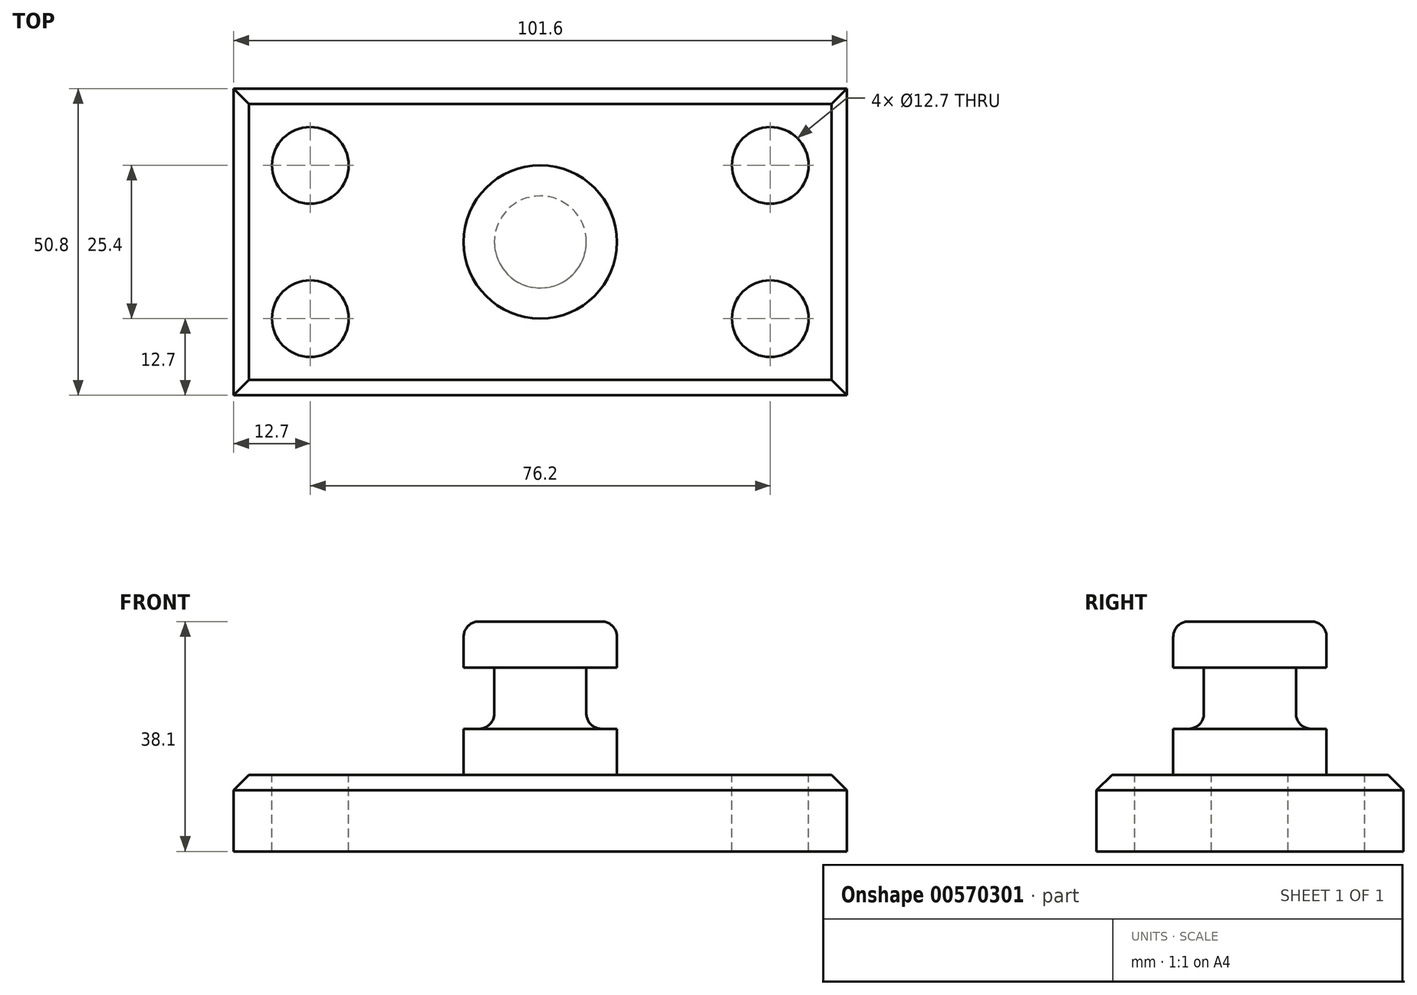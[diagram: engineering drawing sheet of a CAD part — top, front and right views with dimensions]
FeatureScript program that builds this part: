
annotation { "Feature Type Name" : "Feature", "Feature Type Description" : "" }
export const myFeature = defineFeature(function(context is Context, id is Id, definition is map)
    precondition{}
    {
        {
            var Q0;
            Q0=qCreatedBy(makeId("Top.planeOp"),FACE);
            var sketch = newSketch(context, id + "F0", { "sketchPlane" : qUnion([Q0])});
            skLineSegment(sketch, "E0.bottom", {"start": v(50.8, -25.4) * mm, "end": v(-50.8, -25.4) * mm});
            skLineSegment(sketch, "E0.top", {"start": v(50.8, 25.4) * mm, "end": v(-50.8, 25.4) * mm});
            skLineSegment(sketch, "E0.left", {"start": v(50.8, -25.4) * mm, "end": v(50.8, 25.4) * mm});
            skLineSegment(sketch, "E0.right", {"start": v(-50.8, -25.4) * mm, "end": v(-50.8, 25.4) * mm});
            skPoint(sketch, "E0.middle", {"position": v(0, 0) * mm});
            skSolve(sketch);
        }
        {
            var Q0;
            Q0 = qSketchRegion(id + "F0", true);
            extrude(context, id + "F1", {"entities" : qUnion([Q0]), "depth" : 12.7 * mm, "offsetDistance" : 25.4 * mm});
        }
        {
            var Q0;
            Q0=makeQuery(id+"F1.opExtrude","CAP_FACE",FACE,{"disambiguationData":[OSD([sQuery(id+"F0.wireOp",EDGE,"E0.bottom"),sQuery(id+"F0.wireOp",EDGE,"E0.top"),sQuery(id+"F0.wireOp",EDGE,"E0.left"),sQuery(id+"F0.wireOp",EDGE,"E0.right")])],"isStart":false});
            var sketch = newSketch(context, id + "F2", { "sketchPlane" : qUnion([Q0])});
            skCircle(sketch, "E1", {"center": v(38.1, 12.7) * mm, "radius": 6.35 * mm});
            skCircle(sketch, "E2", {"center": v(38.1, -12.7) * mm, "radius": 6.35 * mm});
            skCircle(sketch, "E3", {"center": v(-38.1, 12.7) * mm, "radius": 6.35 * mm});
            skCircle(sketch, "E4", {"center": v(-38.1, -12.7) * mm, "radius": 6.35 * mm});
            skSolve(sketch);
        }
        {
            var Q0;
            Q0 = qSketchRegion(id + "F2", true);
            extrude(context, id + "F3", {"entities" : qUnion([Q0]), "operationType" : NewBodyOperationType.REMOVE, "endBound" : BoundingType.THROUGH_ALL, "oppositeDirection" : true, "depth" : 25.4 * mm, "offsetDistance" : 25.4 * mm});
        }
        {
            var Q0;
            Q0=qCreatedBy(makeId("Front.planeOp"),FACE);
            var sketch = newSketch(context, id + "F4", { "sketchPlane" : qUnion([Q0])});
            skLineSegment(sketch, "E5.bottom", {"start": v(0, 12.7) * mm, "end": v(12.7, 12.7) * mm});
            skLineSegment(sketch, "E5.top", {"start": v(0, 38.1) * mm, "end": v(12.7, 38.1) * mm});
            skLineSegment(sketch, "E5.left", {"start": v(0, 12.7) * mm, "end": v(0, 38.1) * mm});
            skLineSegment(sketch, "E5.right", {"start": v(12.7, 12.7) * mm, "end": v(12.7, 38.1) * mm});
            skSolve(sketch);
        }
        {
            var Q0;
            Q0 = qSketchRegion(id + "F4", true);
            var Q1;
            Q1=sQuery(id+"F4.wireOp",EDGE,"E5.left");
            revolve(context, id + "F5", {"operationType" : NewBodyOperationType.ADD, "entities" : qUnion([Q0]), "axis" : qUnion([Q1]), "revolveType" : RevolveType.FULL});
        }
        {
            var Q0;
            Q0=qCreatedBy(makeId("Front.planeOp"),FACE);
            var sketch = newSketch(context, id + "F6", { "sketchPlane" : qUnion([Q0])});
            skLineSegment(sketch, "E6.bottom", {"start": v(12.7, 20.32) * mm, "end": v(7.62, 20.32) * mm});
            skLineSegment(sketch, "E6.top", {"start": v(12.7, 30.48) * mm, "end": v(7.62, 30.48) * mm});
            skLineSegment(sketch, "E6.left", {"start": v(7.62, 20.32) * mm, "end": v(7.62, 30.48) * mm});
            skLineSegment(sketch, "E6.right", {"start": v(12.7, 20.32) * mm, "end": v(12.7, 30.48) * mm});
            skSolve(sketch);
        }
        {
            var Q0;
            Q0 = qSketchRegion(id + "F6", true);
            var Q1;
            Q1=makeQuery(id+"F5.opRevolve","SWEPT_FACE",FACE,{"disambiguationData":[OSD([sQuery(id+"F4.wireOp",EDGE,"E5.right")])]});
            revolve(context, id + "F7", {"operationType" : NewBodyOperationType.REMOVE, "entities" : qUnion([Q0]), "axis" : qUnion([Q1]), "revolveType" : RevolveType.FULL, "oppositeDirection" : true});
        }
        {
            var Q0;
            Q0=makeQuery(id+"F5.opRevolve","SWEPT_EDGE",EDGE,{"disambiguationData":[OSD([sQuery(id+"F4.wireOp",EDGE,"E5.top"),sQuery(id+"F4.wireOp",EDGE,"E5.right")])]});
            var Q1;
            Q1=makeQuery(id+"F7.boolean.opBoolean","COPY",EDGE,{"derivedFrom":makeQuery(id+"F7.opRevolve","SWEPT_EDGE",EDGE,{"disambiguationData":[OSD([sQuery(id+"F6.wireOp",EDGE,"E6.bottom"),sQuery(id+"F6.wireOp",EDGE,"E6.left")])]})});
            fillet(context, id + "F8", {"entities" : qUnion([Q0, Q1]), "radius" : 2.54 * mm, "tangentPropagation" : true, "allowEdgeOverflow" : false});
        }
        {
            var Q0;
            Q0=makeQuery(id+"F1.opExtrude","CAP_EDGE",EDGE,{"disambiguationData":[OSD([sQuery(id+"F0.wireOp",EDGE,"E0.bottom")])],"isStart":false});
            var Q1;
            Q1=makeQuery(id+"F1.opExtrude","CAP_EDGE",EDGE,{"disambiguationData":[OSD([sQuery(id+"F0.wireOp",EDGE,"E0.left")])],"isStart":false});
            var Q2;
            Q2=makeQuery(id+"F1.opExtrude","CAP_EDGE",EDGE,{"disambiguationData":[OSD([sQuery(id+"F0.wireOp",EDGE,"E0.top")])],"isStart":false});
            var Q3;
            Q3=makeQuery(id+"F1.opExtrude","CAP_EDGE",EDGE,{"disambiguationData":[OSD([sQuery(id+"F0.wireOp",EDGE,"E0.right")])],"isStart":false});
            chamfer(context, id + "F9", {"entities" : qUnion([Q0, Q1, Q2, Q3]), "chamferType" : ChamferType.OFFSET_ANGLE, "width" : 2.54 * mm, "oppositeDirection" : false, "angle" : 45 * degree, "tangentPropagation" : true});
        }
    });
